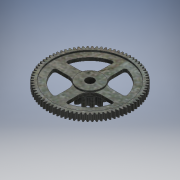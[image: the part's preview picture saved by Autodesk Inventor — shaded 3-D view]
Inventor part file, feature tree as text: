
AUTODESK INVENTOR PART (.ipt)
format: ipt  version: 2020.2 (Build 242310000, 310)  size: 2,364,416 bytes
history: native  units: mm
features: sketch x6, other x5, extrude x5, fillet x3, projected_geometry x2, hole x1
ambient origin geometry x8: Origin, YZ Plane, XZ Plane, XY Plane, X Axis, Y Axis, Z Axis, Center Point
bodies: Body1 (feature_tree)
feature tree (22):
  other  "ソリッド1"
  sketch  "スケッチ1"
  extrude  "押し出し1"  Depth=3.0mm TaperAngle=0.0deg
  extrude  "押し出し2"  Depth=5.0mm TaperAngle=0.0deg
  hole  "穴1"  [1 undecoded]
  extrude  "押し出し3"  Depth=36.5mm
  extrude  "押し出し4"  Depth=0.75mm TaperAngle=0.0deg
  fillet  "フィレット1"  Radius=12.0mm
  extrude  "押し出し5"  Depth=36.5mm
  fillet  "フィレット2"  Radius=0.75mm
  fillet  "フィレット3"  Radius=0.5mm
  sketch  "スケッチ6"
  sketch  "スケッチ2"
  sketch  "スケッチ3"
  sketch  "スケッチ4"
  sketch  "スケッチ5"
  projected_geometry  "投影ループ1"
  projected_geometry  "投影ループ2"
  other  "断面エッジを投影1"
  other  "断面エッジを投影2"
  other  "断面エッジを投影3"
  other  "断面エッジを投影4"
note: 1 required parameter value undecoded (feature->parameter linkage not recoverable at this tier; creation-order binding heuristic only, values carry confidence <= 0.55)
